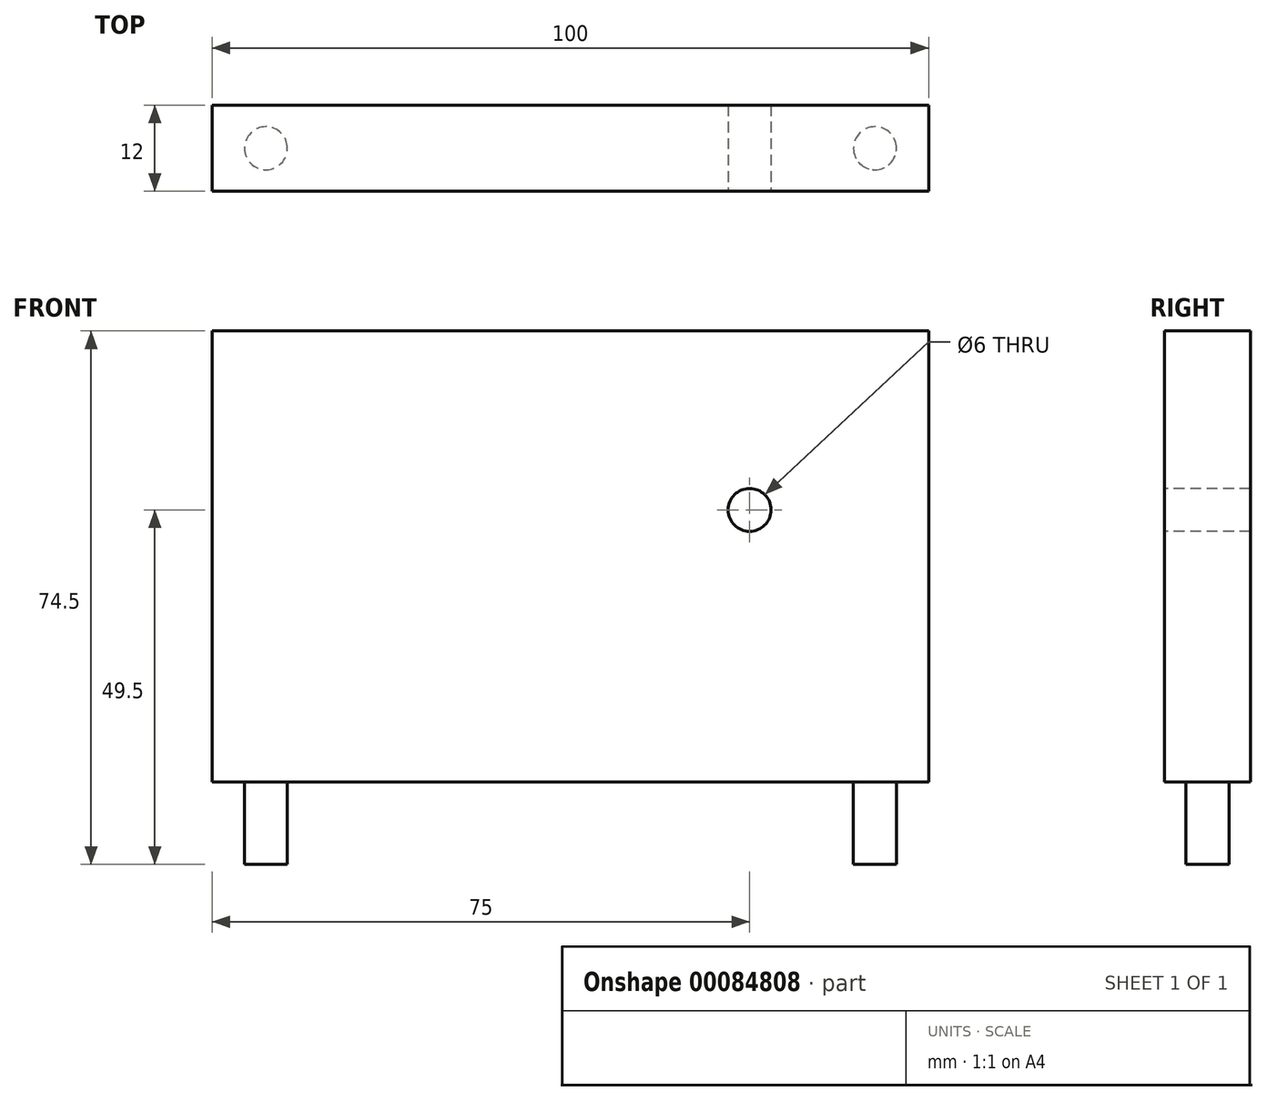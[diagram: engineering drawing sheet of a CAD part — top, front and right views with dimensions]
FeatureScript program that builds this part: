
annotation { "Feature Type Name" : "Feature", "Feature Type Description" : "" }
export const myFeature = defineFeature(function(context is Context, id is Id, definition is map)
    precondition{}
    {
        {
            var Q0;
            Q0=qCreatedBy(makeId("Front.planeOp"),FACE);
            var sketch = newSketch(context, id + "F0", { "sketchPlane" : qUnion([Q0])});
            skLineSegment(sketch, "E0.bottom", {"start": v(0, 0) * mm, "end": v(100, 0) * mm});
            skLineSegment(sketch, "E0.top", {"start": v(0, 63) * mm, "end": v(100, 63) * mm});
            skLineSegment(sketch, "E0.left", {"start": v(0, 0) * mm, "end": v(0, 63) * mm});
            skLineSegment(sketch, "E0.right", {"start": v(100, 0) * mm, "end": v(100, 63) * mm});
            skSolve(sketch);
        }
        {
            var Q0;
            Q0=qSketchRegion(id+"F0",true);
            extrude(context, id + "F1", {"entities" : qUnion([Q0]), "depth" : 12 * mm});
        }
        {
            var Q0;
            Q0=makeQuery(id+"F1.opExtrude","SWEPT_FACE",FACE,{"disambiguationData":[OSD([sQuery(id+"F0.wireOp",EDGE,"E0.bottom")])]});
            var sketch = newSketch(context, id + "F2", { "sketchPlane" : qUnion([Q0])});
            skLineSegment(sketch, "E1", {"start": v(0, 6) * mm, "end": v(100, 6) * mm, "construction": true});
            skCircle(sketch, "E2", {"center": v(7.5, 6) * mm, "radius": 3 * mm});
            skCircle(sketch, "E3", {"center": v(92.5, 6) * mm, "radius": 3 * mm});
            skLineSegment(sketch, "E4", {"start": v(50, 12) * mm, "end": v(50, 0) * mm, "construction": true});
            skLineSegment(sketch, "E5", {"start": v(7.5, 6) * mm, "end": v(92.5, 6) * mm, "construction": true});
            skLineSegment(sketch, "E6", {"start": v(50, 6) * mm, "end": v(50, 12) * mm, "construction": true});
            skSolve(sketch);
        }
        {
            var Q0;
            Q0=qSketchRegion(id+"F2",true);
            extrude(context, id + "F3", {"entities" : qUnion([Q0]), "operationType" : NewBodyOperationType.ADD, "depth" : 11.5 * mm});
        }
        {
            var Q0;
            Q0=makeQuery(id+"F1.opExtrude","CAP_FACE",FACE,{"disambiguationData":[OSD([sQuery(id+"F0.wireOp",EDGE,"E0.bottom"),sQuery(id+"F0.wireOp",EDGE,"E0.top"),sQuery(id+"F0.wireOp",EDGE,"E0.left"),sQuery(id+"F0.wireOp",EDGE,"E0.right")])],"isStart":false});
            var sketch = newSketch(context, id + "F4", { "sketchPlane" : qUnion([Q0])});
            skCircle(sketch, "E7", {"center": v(75, 38) * mm, "radius": 3 * mm});
            skLineSegment(sketch, "E8", {"start": v(50, 0) * mm, "end": v(50, 63) * mm, "construction": true});
            skSolve(sketch);
        }
        {
            var Q0;
            Q0=qSketchRegion(id+"F4",true);
            extrude(context, id + "F5", {"entities" : qUnion([Q0]), "operationType" : NewBodyOperationType.REMOVE, "endBound" : BoundingType.THROUGH_ALL, "oppositeDirection" : true, "depth" : 25 * mm});
        }
    });
